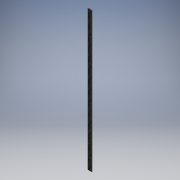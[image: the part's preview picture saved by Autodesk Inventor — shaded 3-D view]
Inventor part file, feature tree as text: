
AUTODESK INVENTOR PART (.ipt)
format: ipt  version: 2018 (Build 220112000, 112)  size: 122,368 bytes
history: native  units: mm
features: extrude x2, sketch x2, other x1
ambient origin geometry x8: Origin, YZ Plane, XZ Plane, XY Plane, X Axis, Y Axis, Z Axis, Center Point
bodies: Body1 (feature_tree)
feature tree (5):
  other  "Sólido1"
  extrude  "Extrusión1"  Depth=75.0mm
  extrude  "Extrusión2"  Depth=10.0mm TaperAngle=0.0deg
  sketch  "Boceto1"  dims[d0=2570.0mm d1=75.0mm]
  sketch  "Boceto2"  dims[d2=10.0mm d3=0.0mm d4=10.0mm d5=214.0mm d6=10.0mm d7=214.0mm d8=10.0mm d9=214.0mm d10=10.0mm d11=214.0mm d12=10.0mm d13=214.0mm d14=215.0mm d15=10.0mm d16=0.0mm]
